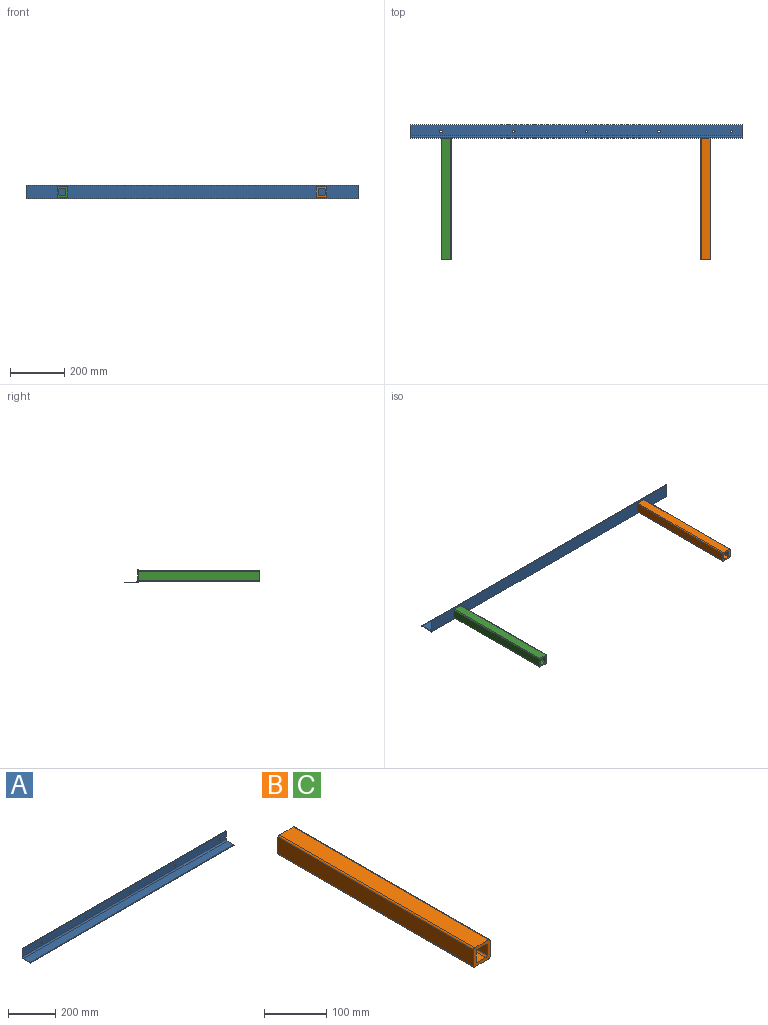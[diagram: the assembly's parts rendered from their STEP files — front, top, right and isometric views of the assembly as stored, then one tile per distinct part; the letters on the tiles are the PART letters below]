
ASSEMBLY  parts=3 mates=2
PART A: 16 faces, bbox 1219.2x50.8x50.8 mm
  f0: plane 50.8x50.8mm, normal (1,0,0), area 320mm2, adj f2,f3,f4,f5,f6,f7,f8,f9
  f1: plane 50.8x50.8mm, normal (-1,0,0), area 320mm2, adj f2,f3,f4,f5,f6,f7,f8,f9
  f2: cylinder r=1.6mm len=1219.2mm, axis (-1,0,0), area 3032.4mm2, adj f0,f1,f3,f10
  f3: plane 1219.2x39.69mm, normal (0,0,1), area 48387mm2, adj f0,f1,f2,f4
  f4: cylinder r=6.35mm len=1219.2mm, axis (-1,0,0), area 12161.1mm2, adj f0,f1,f3,f5
  f5: plane 1219.2x39.69mm, normal (0,-1,0), area 48030.7mm2, adj f0,f1,f4,f6,f11,f12,f13,f14
  f6: cylinder r=1.6mm len=1219.2mm, axis (-1,0,0), area 3032.4mm2, adj f0,f1,f5,f7
  f7: plane 1219.2x1.59mm, normal (0,0,1), area 1935.5mm2, adj f0,f1,f6,f8
  f8: plane 1219.2x50.8mm, normal (0,1,0), area 61579.1mm2, adj f0,f1,f7,f9,f11,f12,f13,f14
  f9: plane 1219.2x50.8mm, normal (0,0,-1), area 61935.4mm2, adj f0,f1,f8,f10
  f10: plane 1219.2x1.59mm, normal (0,-1,0), area 1935.5mm2, adj f0,f1,f2,f9
  f11: cylinder r=4.76mm len=9.53mm, axis (0,1,0), area 95mm2, adj f5,f8
  f12: cylinder r=4.76mm len=9.53mm, axis (0,1,0), area 95mm2, adj f5,f8
  f13: cylinder r=4.76mm len=9.53mm, axis (0,1,0), area 95mm2, adj f5,f8
  f14: cylinder r=4.76mm len=9.53mm, axis (0,1,0), area 95mm2, adj f5,f8
  f15: cylinder r=4.76mm len=9.53mm, axis (0,1,0), area 95mm2, adj f5,f8
PART B: 18 faces, bbox 38.1x444.5x38.1 mm
  f0: plane 444.5x31.75mm, normal (1,0,0), area 14112.9mm2, adj f1,f15,f16,f17
  f1: cylinder r=3.17mm len=444.5mm, axis (0,1,0), area 2216.8mm2, adj f0,f2,f16,f17
  f2: plane 444.5x31.75mm, normal (0,0,1), area 14112.9mm2, adj f1,f3,f16,f17
  f3: cylinder r=3.17mm len=444.5mm, axis (0,1,0), area 2216.8mm2, adj f2,f4,f16,f17
  f4: plane 444.5x31.75mm, normal (-1,0,0), area 14112.9mm2, adj f3,f5,f16,f17
  f5: cylinder r=3.17mm len=444.5mm, axis (0,1,0), area 2216.8mm2, adj f4,f6,f16,f17
  f6: plane 444.5x31.75mm, normal (0,0,-1), area 14112.9mm2, adj f5,f15,f16,f17
  f7: cylinder r=3.17mm len=444.5mm, axis (0,1,0), area 2216.8mm2, adj f8,f14,f16,f17
  f8: plane 444.5x19.05mm, normal (0,0,-1), area 8467.7mm2, adj f7,f9,f16,f17
  f9: cylinder r=3.17mm len=444.5mm, axis (0,1,0), area 2216.8mm2, adj f8,f10,f16,f17
  f10: plane 444.5x19.05mm, normal (-1,0,0), area 8467.7mm2, adj f9,f11,f16,f17
  f11: cylinder r=3.17mm len=444.5mm, axis (0,1,0), area 2216.8mm2, adj f10,f12,f16,f17
  f12: plane 444.5x19.05mm, normal (0,0,1), area 8467.7mm2, adj f11,f13,f16,f17
  f13: cylinder r=3.17mm len=444.5mm, axis (0,1,0), area 2216.8mm2, adj f12,f14,f16,f17
  f14: plane 444.5x19.05mm, normal (1,0,0), area 8467.7mm2, adj f7,f13,f16,f17
  f15: cylinder r=3.17mm len=444.5mm, axis (0,1,0), area 2216.8mm2, adj f0,f6,f16,f17
  f16: plane 38.1x38.1mm, normal (0,-1,0), area 806.5mm2, adj f0,f1,f2,f3,f4,f5,f6,f7
  f17: plane 38.1x38.1mm, normal (0,1,0), area 806.5mm2, adj f0,f1,f2,f3,f4,f5,f6,f7
PART C: same geometry as B
PLACE A rot(axis=(-1,0,0),90deg) t=(150.15,178.46,-105.64)mm
PLACE B t=(17.23,178.46,-80.49)mm
PLACE C rot(axis=(1,0,0),180deg) t=(-935.27,-266.04,-79.99)mm
MATE fastened A.f9 <-> C.f16  axis (0,-1,0) through (-1069.05,178.46,-80.24)mm
MATE fastened A.f9 <-> B.f17  axis (0,-1,0) through (150.15,178.46,-80.24)mm
